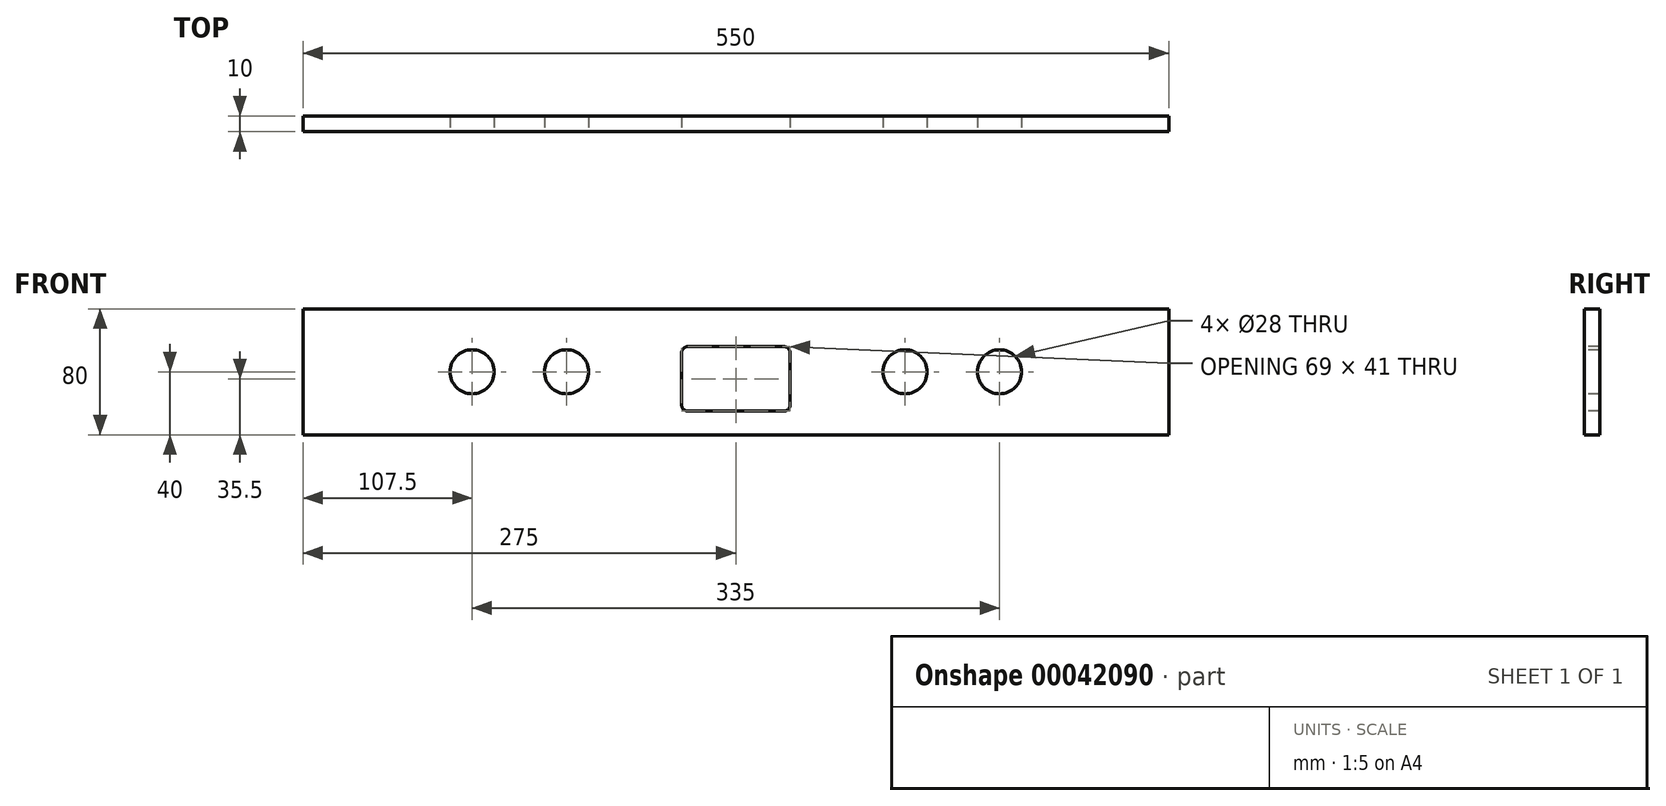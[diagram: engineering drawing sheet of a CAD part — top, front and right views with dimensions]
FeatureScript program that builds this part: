
annotation { "Feature Type Name" : "Feature", "Feature Type Description" : "" }
export const myFeature = defineFeature(function(context is Context, id is Id, definition is map)
    precondition{}
    {
        {
            var Q0;
            Q0=qCreatedBy(makeId("Front.planeOp"),FACE);
            var sketch = newSketch(context, id + "F0", { "sketchPlane" : qUnion([Q0])});
            skLineSegment(sketch, "E0.rect.bottom", {"start": v(275, 40) * mm, "end": v(-275, 40) * mm});
            skLineSegment(sketch, "E0.rect.top", {"start": v(275, -40) * mm, "end": v(-275, -40) * mm});
            skLineSegment(sketch, "E0.rect.left", {"start": v(275, 40) * mm, "end": v(275, -40) * mm});
            skLineSegment(sketch, "E0.rect.right", {"start": v(-275, 40) * mm, "end": v(-275, -40) * mm});
            skPoint(sketch, "E0.rect.middle", {"position": v(0, 0) * mm});
            skLineSegment(sketch, "E1", {"start": v(0, 49.04) * mm, "end": v(0, -52.88) * mm, "construction": true});
            skLineSegment(sketch, "E2", {"start": v(-137.5, 48.18) * mm, "end": v(-137.5, -52.02) * mm, "construction": true});
            skLineSegment(sketch, "E3", {"start": v(-167.5, 47.75) * mm, "end": v(-167.5, -51.6) * mm, "construction": true});
            skLineSegment(sketch, "E4", {"start": v(-284.83, 0) * mm, "end": v(283.41, 0) * mm, "construction": true});
            skCircle(sketch, "E5", {"center": v(-167.5, 0) * mm, "radius": 14 * mm});
            skCircle(sketch, "E6.MirrorC", {"center": v(-107.5, 0) * mm, "radius": 14 * mm});
            skCircle(sketch, "E7.MirrorC", {"center": v(167.5, 0) * mm, "radius": 14 * mm});
            skCircle(sketch, "E8.MirrorC", {"center": v(107.5, 0) * mm, "radius": 14 * mm});
            skLineSegment(sketch, "E9.bottom", {"start": v(-34.5, 16) * mm, "end": v(34.5, 16) * mm});
            skLineSegment(sketch, "E9.top", {"start": v(-34.5, -25) * mm, "end": v(34.5, -25) * mm});
            skLineSegment(sketch, "E9.left", {"start": v(-34.5, 16) * mm, "end": v(-34.5, -25) * mm});
            skLineSegment(sketch, "E9.right", {"start": v(34.5, 16) * mm, "end": v(34.5, -25) * mm});
            skSolve(sketch);
        }
        {
            var Q0;
            Q0=makeQuery(id+"F0.imprint","IMPRINT",FACE,{"disambiguationData":[TD([[makeQuery(id+"F0.imprint","IMPRINT",EDGE,{"derivedFrom":sQuery(id+"F0.wireOp",EDGE,"E0.rect.bottom")}),1.0]])]});
            extrude(context, id + "F1", {"entities" : qUnion([Q0]), "oppositeDirection" : true, "depth" : 10 * mm});
        }
        {
            var Q0;
            Q0=makeQuery(id+"F1.opExtrude","SWEPT_EDGE",EDGE,{"disambiguationData":[OSD([sQuery(id+"F0.wireOp",EDGE,"E9.bottom"),sQuery(id+"F0.wireOp",EDGE,"E9.left")])]});
            var Q1;
            Q1=makeQuery(id+"F1.opExtrude","SWEPT_EDGE",EDGE,{"disambiguationData":[OSD([sQuery(id+"F0.wireOp",EDGE,"E9.bottom"),sQuery(id+"F0.wireOp",EDGE,"E9.right")])]});
            var Q2;
            Q2=makeQuery(id+"F1.opExtrude","SWEPT_EDGE",EDGE,{"disambiguationData":[OSD([sQuery(id+"F0.wireOp",EDGE,"E9.top"),sQuery(id+"F0.wireOp",EDGE,"E9.right")])]});
            var Q3;
            Q3=makeQuery(id+"F1.opExtrude","SWEPT_EDGE",EDGE,{"disambiguationData":[OSD([sQuery(id+"F0.wireOp",EDGE,"E9.top"),sQuery(id+"F0.wireOp",EDGE,"E9.left")])]});
            fillet(context, id + "F2", {"entities" : qUnion([Q0, Q1, Q2, Q3]), "radius" : 4 * mm, "tangentPropagation" : true, "allowEdgeOverflow" : false});
        }
    });
